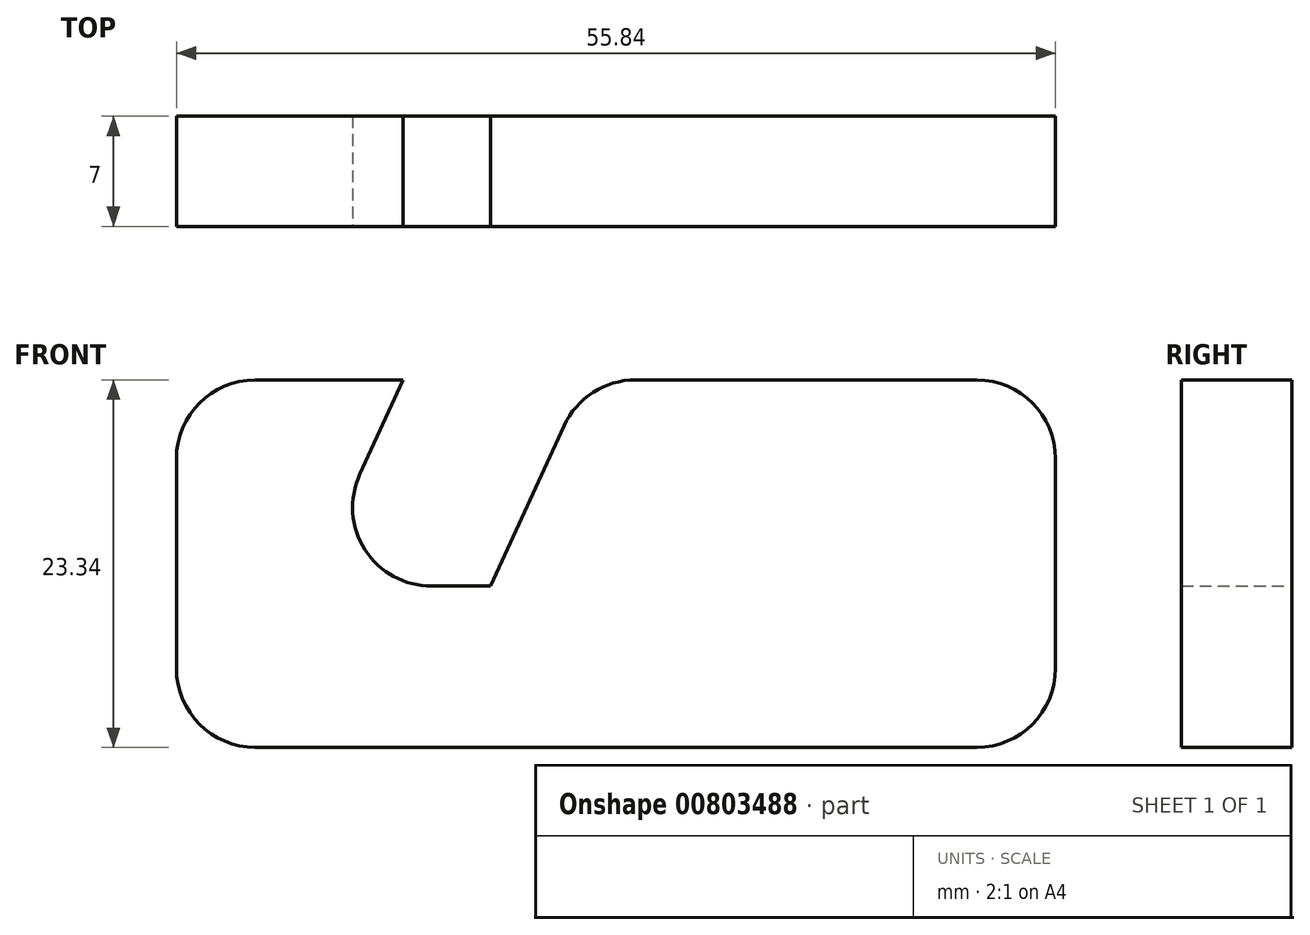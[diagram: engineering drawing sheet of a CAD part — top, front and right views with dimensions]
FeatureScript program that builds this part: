
annotation { "Feature Type Name" : "Feature", "Feature Type Description" : "" }
export const myFeature = defineFeature(function(context is Context, id is Id, definition is map)
    precondition{}
    {
        {
            var Q0;
            Q0=qCreatedBy(makeId("Front.planeOp"),FACE);
            var sketch = newSketch(context, id + "F0", { "sketchPlane" : qUnion([Q0])});
            skLineSegment(sketch, "E0.bottom", {"start": v(0, 0) * mm, "end": v(55.84, 0) * mm});
            skLineSegment(sketch, "E0.top", {"start": v(0, 23.34) * mm, "end": v(14.4, 23.34) * mm});
            skLineSegment(sketch, "E0.left", {"start": v(0, 0) * mm, "end": v(0, 23.34) * mm});
            skLineSegment(sketch, "E0.right", {"start": v(55.84, 0) * mm, "end": v(55.84, 23.34) * mm});
            skLineSegment(sketch, "E1", {"start": v(14.4, 23.34) * mm, "end": v(8.4, 10.24) * mm});
            skLineSegment(sketch, "E2", {"start": v(8.4, 10.24) * mm, "end": v(19.95, 10.24) * mm});
            skLineSegment(sketch, "E3", {"start": v(19.95, 10.24) * mm, "end": v(25.95, 23.34) * mm});
            skLineSegment(sketch, "E4.trimOffspring", {"start": v(25.95, 23.34) * mm, "end": v(55.84, 23.34) * mm});
            skSolve(sketch);
        }
        {
            var Q0;
            Q0 = qSketchRegion(id + "F0", true);
            extrude(context, id + "F1", {"entities" : qUnion([Q0]), "depth" : 7 * mm, "offsetDistance" : 25 * mm});
        }
        {
            var Q0;
            Q0=makeQuery(id+"F1.opExtrude","SWEPT_EDGE",EDGE,{"disambiguationData":[OSD([sQuery(id+"F0.wireOp",EDGE,"E0.right"),sQuery(id+"F0.wireOp",EDGE,"E4.trimOffspring")])]});
            var Q1;
            Q1=makeQuery(id+"F1.opExtrude","SWEPT_EDGE",EDGE,{"disambiguationData":[OSD([sQuery(id+"F0.wireOp",EDGE,"E0.bottom"),sQuery(id+"F0.wireOp",EDGE,"E0.right")])]});
            var Q2;
            Q2=makeQuery(id+"F1.opExtrude","SWEPT_EDGE",EDGE,{"disambiguationData":[OSD([sQuery(id+"F0.wireOp",EDGE,"E3"),sQuery(id+"F0.wireOp",EDGE,"E4.trimOffspring")])]});
            var Q3;
            Q3=makeQuery(id+"F1.opExtrude","SWEPT_EDGE",EDGE,{"disambiguationData":[OSD([sQuery(id+"F0.wireOp",EDGE,"E0.bottom"),sQuery(id+"F0.wireOp",EDGE,"E0.left")])]});
            var Q4;
            Q4=makeQuery(id+"F1.opExtrude","SWEPT_EDGE",EDGE,{"disambiguationData":[OSD([sQuery(id+"F0.wireOp",EDGE,"E1"),sQuery(id+"F0.wireOp",EDGE,"E2")])]});
            var Q5;
            Q5=makeQuery(id+"F1.opExtrude","SWEPT_EDGE",EDGE,{"disambiguationData":[OSD([sQuery(id+"F0.wireOp",EDGE,"E0.top"),sQuery(id+"F0.wireOp",EDGE,"E0.left")])]});
            fillet(context, id + "F2", {"entities" : qUnion([Q0, Q1, Q2, Q3, Q4, Q5]), "radius" : 5 * mm, "tangentPropagation" : true, "allowEdgeOverflow" : false});
        }
    });
